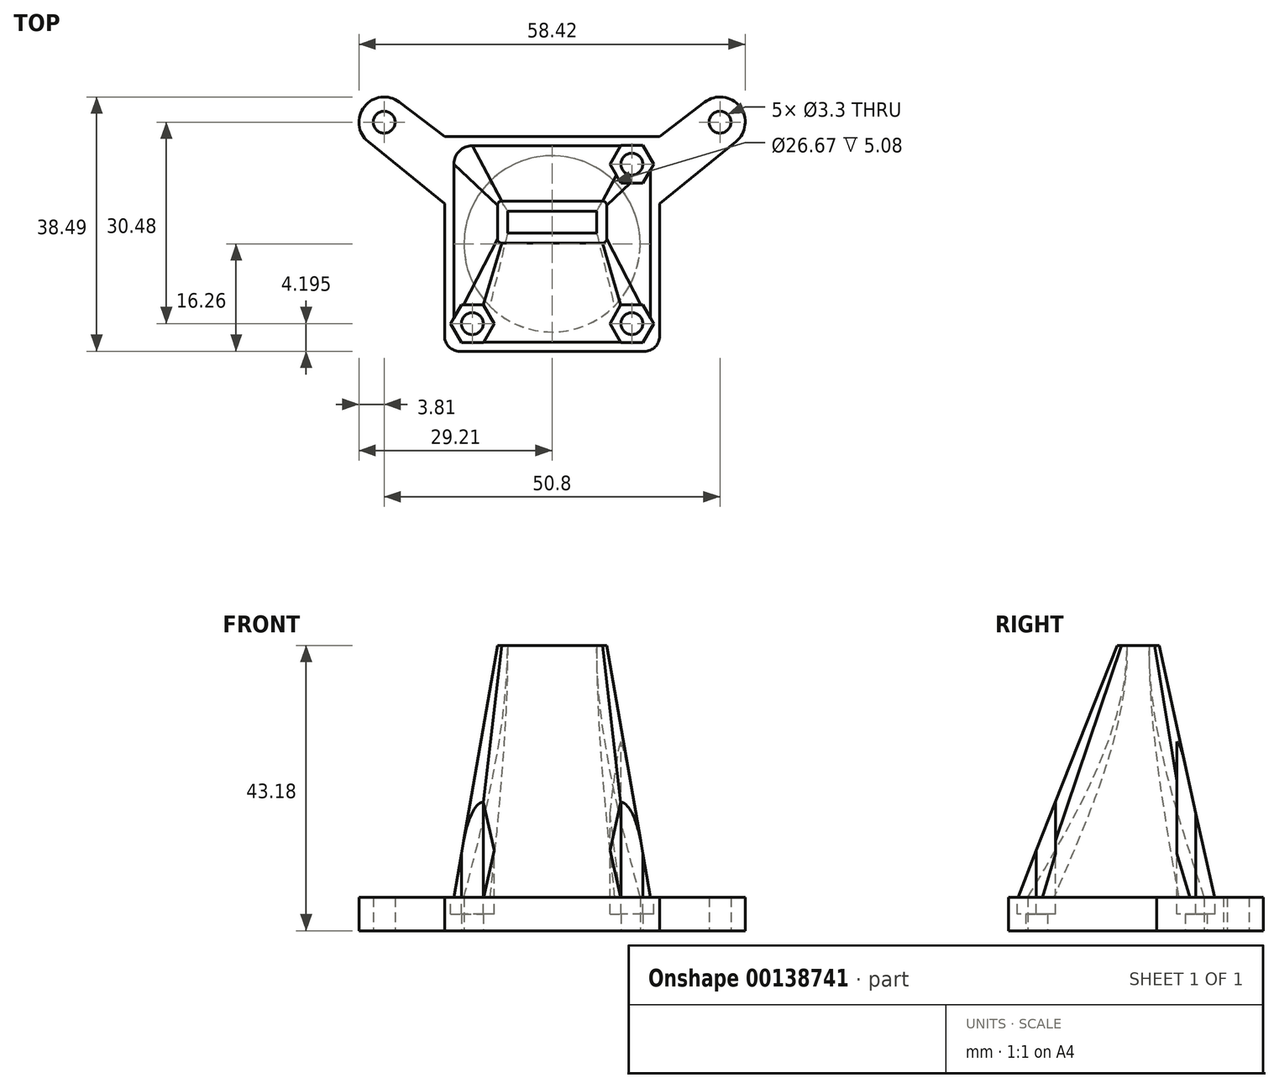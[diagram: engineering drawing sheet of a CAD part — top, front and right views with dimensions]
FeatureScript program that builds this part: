
annotation { "Feature Type Name" : "Feature", "Feature Type Description" : "" }
export const myFeature = defineFeature(function(context is Context, id is Id, definition is map)
    precondition{}
    {
        {
            var Q0;
            Q0=qCreatedBy(makeId("Top.planeOp"),FACE);
            var sketch = newSketch(context, id + "F0", { "sketchPlane" : qUnion([Q0])});
            skCircle(sketch, "E0", {"center": v(0, 0) * mm, "radius": 13.34 * mm});
            skLineSegment(sketch, "E1.bottom", {"start": v(-16.26, 16.26) * mm, "end": v(16.26, 16.26) * mm});
            skLineSegment(sketch, "E1.top", {"start": v(-13.97, -16.26) * mm, "end": v(13.97, -16.26) * mm});
            skLineSegment(sketch, "E1.left", {"start": v(-16.26, 6.1) * mm, "end": v(-16.26, -13.97) * mm});
            skLineSegment(sketch, "E1.right", {"start": v(16.26, 6.1) * mm, "end": v(16.26, -13.97) * mm});
            skCircle(sketch, "E2", {"center": v(12.07, -12.07) * mm, "radius": 1.65 * mm});
            skCircle(sketch, "E3", {"center": v(-12.07, -12.07) * mm, "radius": 1.65 * mm});
            skCircle(sketch, "E4", {"center": v(12.07, 12.06) * mm, "radius": 1.65 * mm});
            skPoint(sketch, "E5.visualSharp", {"position": v(16.26, -16.26) * mm});
            skArc(sketch, "E5.filletArc", {"start": v(13.97, -16.26) * mm, "mid": v(15.59, -15.59) * mm, "end": v(16.26, -13.97) * mm});
            skPoint(sketch, "E6.visualSharp", {"position": v(-16.26, -16.26) * mm});
            skArc(sketch, "E6.filletArc", {"start": v(-16.26, -13.97) * mm, "mid": v(-15.59, -15.59) * mm, "end": v(-13.97, -16.26) * mm});
            skCircle(sketch, "E7", {"center": v(25.4, 18.41) * mm, "radius": 1.65 * mm});
            skCircle(sketch, "E8", {"center": v(-25.4, 18.41) * mm, "radius": 1.65 * mm});
            skArc(sketch, "E9", {"start": v(27.8, 15.46) * mm, "mid": v(28.4, 20.77) * mm, "end": v(23.1, 21.45) * mm});
            skArc(sketch, "E10", {"start": v(-23.1, 21.45) * mm, "mid": v(-28.4, 20.77) * mm, "end": v(-27.8, 15.46) * mm});
            skLineSegment(sketch, "E11", {"start": v(16.26, 16.26) * mm, "end": v(23.1, 21.45) * mm});
            skLineSegment(sketch, "E12", {"start": v(16.26, 6.1) * mm, "end": v(27.8, 15.46) * mm});
            skLineSegment(sketch, "E13", {"start": v(-16.26, 16.26) * mm, "end": v(-23.1, 21.45) * mm});
            skLineSegment(sketch, "E14", {"start": v(-16.26, 6.1) * mm, "end": v(-27.8, 15.46) * mm});
            skSolve(sketch);
        }
        {
            var Q0;
            Q0 = qSketchRegion(id + "F0", true);
            extrude(context, id + "F1", {"entities" : qUnion([Q0]), "depth" : 5.08 * mm});
        }
        {
            var Q0;
            Q0=qCreatedBy(makeId("Top.planeOp"),FACE);
            cPlane(context, id + "F2", {"entities" : qUnion([Q0]), "cplaneType" : CPlaneType.OFFSET, "offset" : 43.18 * mm, "width" : 152.4 * mm, "height" : 152.4 * mm});
        }
        {
            var Q0;
            Q0=qCreatedBy(id+"F2.planeOp",FACE);
            var sketch = newSketch(context, id + "F3", { "sketchPlane" : qUnion([Q0])});
            skLineSegment(sketch, "E15.bottom", {"start": v(7.62, 0.13) * mm, "end": v(-7.62, 0.13) * mm});
            skLineSegment(sketch, "E15.top", {"start": v(7.62, 6.48) * mm, "end": v(-7.62, 6.48) * mm});
            skLineSegment(sketch, "E15.left", {"start": v(8.26, 0.76) * mm, "end": v(8.26, 5.84) * mm});
            skLineSegment(sketch, "E15.right", {"start": v(-8.26, 0.76) * mm, "end": v(-8.26, 5.84) * mm});
            skPoint(sketch, "E15.middle", {"position": v(0, 3.3) * mm});
            skPoint(sketch, "E16.visualSharp", {"position": v(-8.26, 6.48) * mm});
            skArc(sketch, "E16.filletArc", {"start": v(-7.62, 6.48) * mm, "mid": v(-8.07, 6.3) * mm, "end": v(-8.26, 5.84) * mm});
            skPoint(sketch, "E17.visualSharp", {"position": v(8.26, 6.48) * mm});
            skArc(sketch, "E17.filletArc", {"start": v(8.26, 5.84) * mm, "mid": v(8.07, 6.3) * mm, "end": v(7.62, 6.48) * mm});
            skPoint(sketch, "E18.visualSharp", {"position": v(8.26, 0.13) * mm});
            skArc(sketch, "E18.filletArc", {"start": v(7.62, 0.13) * mm, "mid": v(8.07, 0.31) * mm, "end": v(8.26, 0.76) * mm});
            skPoint(sketch, "E19.visualSharp", {"position": v(-8.26, 0.13) * mm});
            skArc(sketch, "E19.filletArc", {"start": v(-8.26, 0.76) * mm, "mid": v(-8.07, 0.31) * mm, "end": v(-7.62, 0.13) * mm});
            skSolve(sketch);
        }
        {
            var Q0;
            Q0=makeQuery(id+"F1.opExtrude","CAP_FACE",FACE,{"disambiguationData":[OSD([sQuery(id+"F0.wireOp",EDGE,"E0"),sQuery(id+"F0.wireOp",EDGE,"E1.bottom"),sQuery(id+"F0.wireOp",EDGE,"E1.top"),sQuery(id+"F0.wireOp",EDGE,"E1.left"),sQuery(id+"F0.wireOp",EDGE,"E1.right"),sQuery(id+"F0.wireOp",EDGE,"E2"),sQuery(id+"F0.wireOp",EDGE,"E3"),sQuery(id+"F0.wireOp",EDGE,"E4"),sQuery(id+"F0.wireOp",EDGE,"E5.filletArc"),sQuery(id+"F0.wireOp",EDGE,"E6.filletArc"),sQuery(id+"F0.wireOp",EDGE,"E7"),sQuery(id+"F0.wireOp",EDGE,"E8"),sQuery(id+"F0.wireOp",EDGE,"E9"),sQuery(id+"F0.wireOp",EDGE,"E10"),sQuery(id+"F0.wireOp",EDGE,"E11"),sQuery(id+"F0.wireOp",EDGE,"E12"),sQuery(id+"F0.wireOp",EDGE,"E13"),sQuery(id+"F0.wireOp",EDGE,"E14")])],"isStart":false});
            var sketch = newSketch(context, id + "F4", { "sketchPlane" : qUnion([Q0])});
            skLineSegment(sketch, "E20.bottom", {"start": v(12.06, 14.86) * mm, "end": v(-12.07, 14.86) * mm});
            skLineSegment(sketch, "E20.top", {"start": v(12.07, -14.86) * mm, "end": v(-12.06, -14.86) * mm});
            skLineSegment(sketch, "E20.left", {"start": v(14.86, 12.07) * mm, "end": v(14.86, -12.06) * mm});
            skLineSegment(sketch, "E20.right", {"start": v(-14.86, 12.06) * mm, "end": v(-14.86, -12.07) * mm});
            skCircle(sketch, "E21", {"center": v(0, 0) * mm, "radius": 13.34 * mm, "construction": true});
            skPoint(sketch, "E22.visualSharp", {"position": v(-14.86, -14.86) * mm});
            skArc(sketch, "E22.filletArc", {"start": v(-14.86, -12.07) * mm, "mid": v(-14.04, -14.04) * mm, "end": v(-12.06, -14.86) * mm});
            skPoint(sketch, "E23.visualSharp", {"position": v(14.86, -14.86) * mm});
            skArc(sketch, "E23.filletArc", {"start": v(12.07, -14.86) * mm, "mid": v(14.04, -14.04) * mm, "end": v(14.86, -12.06) * mm});
            skPoint(sketch, "E24.visualSharp", {"position": v(14.86, 14.86) * mm});
            skArc(sketch, "E24.filletArc", {"start": v(14.86, 12.07) * mm, "mid": v(14.04, 14.04) * mm, "end": v(12.06, 14.86) * mm});
            skPoint(sketch, "E25.visualSharp", {"position": v(-14.86, 14.86) * mm});
            skArc(sketch, "E25.filletArc", {"start": v(-12.07, 14.86) * mm, "mid": v(-14.04, 14.04) * mm, "end": v(-14.86, 12.06) * mm});
            skSolve(sketch);
        }
        {
            var Q1;
            Q1 = qSketchRegion(id + "F3", true);
            var Q2;
            Q2 = qSketchRegion(id + "F4", true);
            loft(context, id + "F5", {"operationType" : NewBodyOperationType.ADD, "sheetProfilesArray" : [{ "sheetProfileEntities" : qUnion([Q1]) }, { "sheetProfileEntities" : qUnion([Q2]) }]});
        }
        {
            var Q0;
            Q0=qCreatedBy(id+"F2.planeOp",FACE);
            var sketch = newSketch(context, id + "F6", { "sketchPlane" : qUnion([Q0])});
            skCircle(sketch, "E26.cCircle", {"center": v(-12.07, -12.07) * mm, "radius": 2.87 * mm, "construction": true});
            skLineSegment(sketch, "E26.0", {"start": v(-8.75, -12.07) * mm, "end": v(-10.4, -14.94) * mm});
            skLineSegment(sketch, "E26.1", {"start": v(-10.4, -14.94) * mm, "end": v(-13.72, -14.94) * mm});
            skLineSegment(sketch, "E26.2", {"start": v(-13.72, -14.94) * mm, "end": v(-15.38, -12.07) * mm});
            skLineSegment(sketch, "E26.3", {"start": v(-15.38, -12.07) * mm, "end": v(-13.72, -9.2) * mm});
            skLineSegment(sketch, "E26.4", {"start": v(-13.72, -9.2) * mm, "end": v(-10.4, -9.2) * mm});
            skLineSegment(sketch, "E26.5", {"start": v(-10.4, -9.2) * mm, "end": v(-8.75, -12.07) * mm});
            skPoint(sketch, "E26.0.midPoint", {"position": v(-9.58, -13.5) * mm});
            skCircle(sketch, "E27.cCircle", {"center": v(12.07, -12.07) * mm, "radius": 2.87 * mm, "construction": true});
            skLineSegment(sketch, "E27.0", {"start": v(13.72, -14.94) * mm, "end": v(10.4, -14.94) * mm});
            skLineSegment(sketch, "E27.1", {"start": v(10.4, -14.94) * mm, "end": v(8.75, -12.07) * mm});
            skLineSegment(sketch, "E27.2", {"start": v(8.75, -12.07) * mm, "end": v(10.4, -9.2) * mm});
            skLineSegment(sketch, "E27.3", {"start": v(10.4, -9.2) * mm, "end": v(13.72, -9.2) * mm});
            skLineSegment(sketch, "E27.4", {"start": v(13.72, -9.2) * mm, "end": v(15.38, -12.06) * mm});
            skLineSegment(sketch, "E27.5", {"start": v(15.38, -12.07) * mm, "end": v(13.72, -14.94) * mm});
            skPoint(sketch, "E27.0.midPoint", {"position": v(12.07, -14.94) * mm});
            skCircle(sketch, "E28.cCircle", {"center": v(12.07, 12.06) * mm, "radius": 2.87 * mm, "construction": true});
            skLineSegment(sketch, "E28.0", {"start": v(13.72, 9.2) * mm, "end": v(10.4, 9.2) * mm});
            skLineSegment(sketch, "E28.1", {"start": v(10.4, 9.2) * mm, "end": v(8.75, 12.06) * mm});
            skLineSegment(sketch, "E28.2", {"start": v(8.75, 12.06) * mm, "end": v(10.4, 14.94) * mm});
            skLineSegment(sketch, "E28.3", {"start": v(10.4, 14.94) * mm, "end": v(13.72, 14.94) * mm});
            skLineSegment(sketch, "E28.4", {"start": v(13.72, 14.94) * mm, "end": v(15.38, 12.06) * mm});
            skLineSegment(sketch, "E28.5", {"start": v(15.38, 12.07) * mm, "end": v(13.72, 9.2) * mm});
            skPoint(sketch, "E28.0.midPoint", {"position": v(12.07, 9.2) * mm});
            skSolve(sketch);
        }
        {
            var Q0;
            Q0 = qSketchRegion(id + "F6", true);
            extrude(context, id + "F7", {"entities" : qUnion([Q0]), "operationType" : NewBodyOperationType.REMOVE, "oppositeDirection" : true, "depth" : 40.64 * mm});
        }
        {
            var Q0;
            Q0=qCreatedBy(id+"F2.planeOp",FACE);
            var sketch = newSketch(context, id + "F8", { "sketchPlane" : qUnion([Q0])});
            skLineSegment(sketch, "E29.bottom", {"start": v(6.73, 1.65) * mm, "end": v(-6.73, 1.65) * mm});
            skLineSegment(sketch, "E29.top", {"start": v(6.73, 4.95) * mm, "end": v(-6.73, 4.95) * mm});
            skLineSegment(sketch, "E29.left", {"start": v(6.73, 1.65) * mm, "end": v(6.73, 4.95) * mm});
            skLineSegment(sketch, "E29.right", {"start": v(-6.73, 1.65) * mm, "end": v(-6.73, 4.95) * mm});
            skSolve(sketch);
        }
        {
            var Q0;
            Q0=makeQuery(id+"F1.opExtrude","CAP_FACE",FACE,{"disambiguationData":[OSD([sQuery(id+"F0.wireOp",EDGE,"E0"),sQuery(id+"F0.wireOp",EDGE,"E1.bottom"),sQuery(id+"F0.wireOp",EDGE,"E1.top"),sQuery(id+"F0.wireOp",EDGE,"E1.left"),sQuery(id+"F0.wireOp",EDGE,"E1.right"),sQuery(id+"F0.wireOp",EDGE,"E2"),sQuery(id+"F0.wireOp",EDGE,"E3"),sQuery(id+"F0.wireOp",EDGE,"E4"),sQuery(id+"F0.wireOp",EDGE,"E5.filletArc"),sQuery(id+"F0.wireOp",EDGE,"E6.filletArc"),sQuery(id+"F0.wireOp",EDGE,"E7"),sQuery(id+"F0.wireOp",EDGE,"E8"),sQuery(id+"F0.wireOp",EDGE,"E9"),sQuery(id+"F0.wireOp",EDGE,"E10"),sQuery(id+"F0.wireOp",EDGE,"E11"),sQuery(id+"F0.wireOp",EDGE,"E12"),sQuery(id+"F0.wireOp",EDGE,"E13"),sQuery(id+"F0.wireOp",EDGE,"E14")])],"isStart":false});
            var sketch = newSketch(context, id + "F9", { "sketchPlane" : qUnion([Q0])});
            skCircle(sketch, "E30", {"center": v(0, 0) * mm, "radius": 13.34 * mm});
            skLineSegment(sketch, "E31", {"start": v(0, 0) * mm, "end": v(0, 6.97) * mm, "construction": true});
            skLineSegment(sketch, "E32", {"start": v(0, 0) * mm, "end": v(9.43, 9.43) * mm, "construction": true});
            skSolve(sketch);
        }
        {
            var Q1;
            Q1 = qSketchRegion(id + "F8", true);
            var Q2;
            Q2 = qSketchRegion(id + "F9", true);
            var Q3;
            Q3=sQuery(id+"F9.wireOp",VERTEX,"E32.end");
            var Q4;
            Q4=sQuery(id+"F8.wireOp",VERTEX,"E29.left.end");
            loft(context, id + "F10", {"operationType" : NewBodyOperationType.REMOVE, "startCondition" : LoftEndDerivativeType.NORMAL_TO_PROFILE, "startMagnitude" : 1, "sheetProfilesArray" : [{ "sheetProfileEntities" : qUnion([Q1]) }, { "sheetProfileEntities" : qUnion([Q2]) }], "matchConnections" : true, "connections" : [{ "connectionEntities" : qUnion([Q3, Q4]), "connectionEdgeQueries" : qUnion([]), "connectionEdgeParameters" : [] }]});
        }
    });
